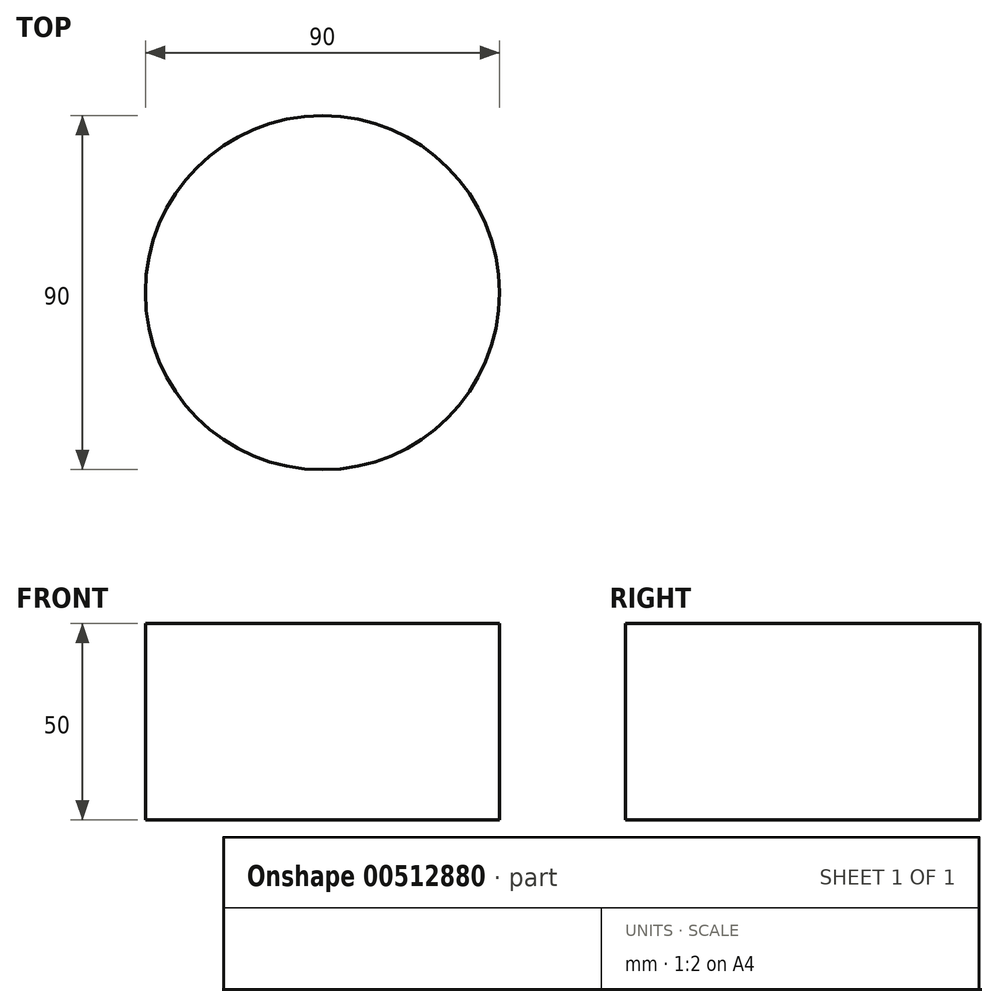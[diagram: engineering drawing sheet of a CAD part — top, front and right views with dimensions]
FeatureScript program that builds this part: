
annotation { "Feature Type Name" : "Feature", "Feature Type Description" : "" }
export const myFeature = defineFeature(function(context is Context, id is Id, definition is map)
    precondition{}
    {
        {
            var Q0;
            Q0=qCreatedBy(makeId("Top.planeOp"),FACE);
            var sketch = newSketch(context, id + "F0", { "sketchPlane" : qUnion([Q0])});
            skCircle(sketch, "E0", {"center": v(0, 0) * mm, "radius": 45 * mm});
            skSolve(sketch);
        }
        {
            var Q0;
            Q0=makeQuery(id+"F0.imprint","IMPRINT",FACE,{"disambiguationData":[TD([[makeQuery(id+"F0.imprint","IMPRINT",EDGE,{"derivedFrom":sQuery(id+"F0.wireOp",EDGE,"E0")}),1.0]])]});
            extrude(context, id + "F1", {"entities" : qUnion([Q0]), "depth" : 50 * mm});
        }
    });
